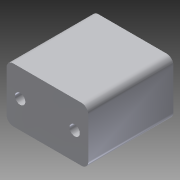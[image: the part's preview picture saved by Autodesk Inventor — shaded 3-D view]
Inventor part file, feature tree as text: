
AUTODESK INVENTOR PART (.ipt)
format: ipt  version: 2014 (Build 180170000, 170)  size: 92,672 bytes
history: native  units: in
note: dims shown in document units (in); Inventor stores cm internally (conversion verified against a paired STEP export)
features: extrude x1, sketch x1
ambient origin geometry x8: Origin, YZ Plane, XZ Plane, XY Plane, X Axis, Y Axis, Z Axis, Center Point
bodies: Solid1 (feature_tree)
feature tree (2):
  extrude  "Extrusion1"  Depth=1.0in
  sketch  "Sketch1"  dims[d0=1.5in d1=1.0in d2=0.19in d3=0.25in d5=0.7874in d7=1.0in d8=0.3937in d10=1.0in d20=0.125in d21=1.5625in d22=0.0in]
